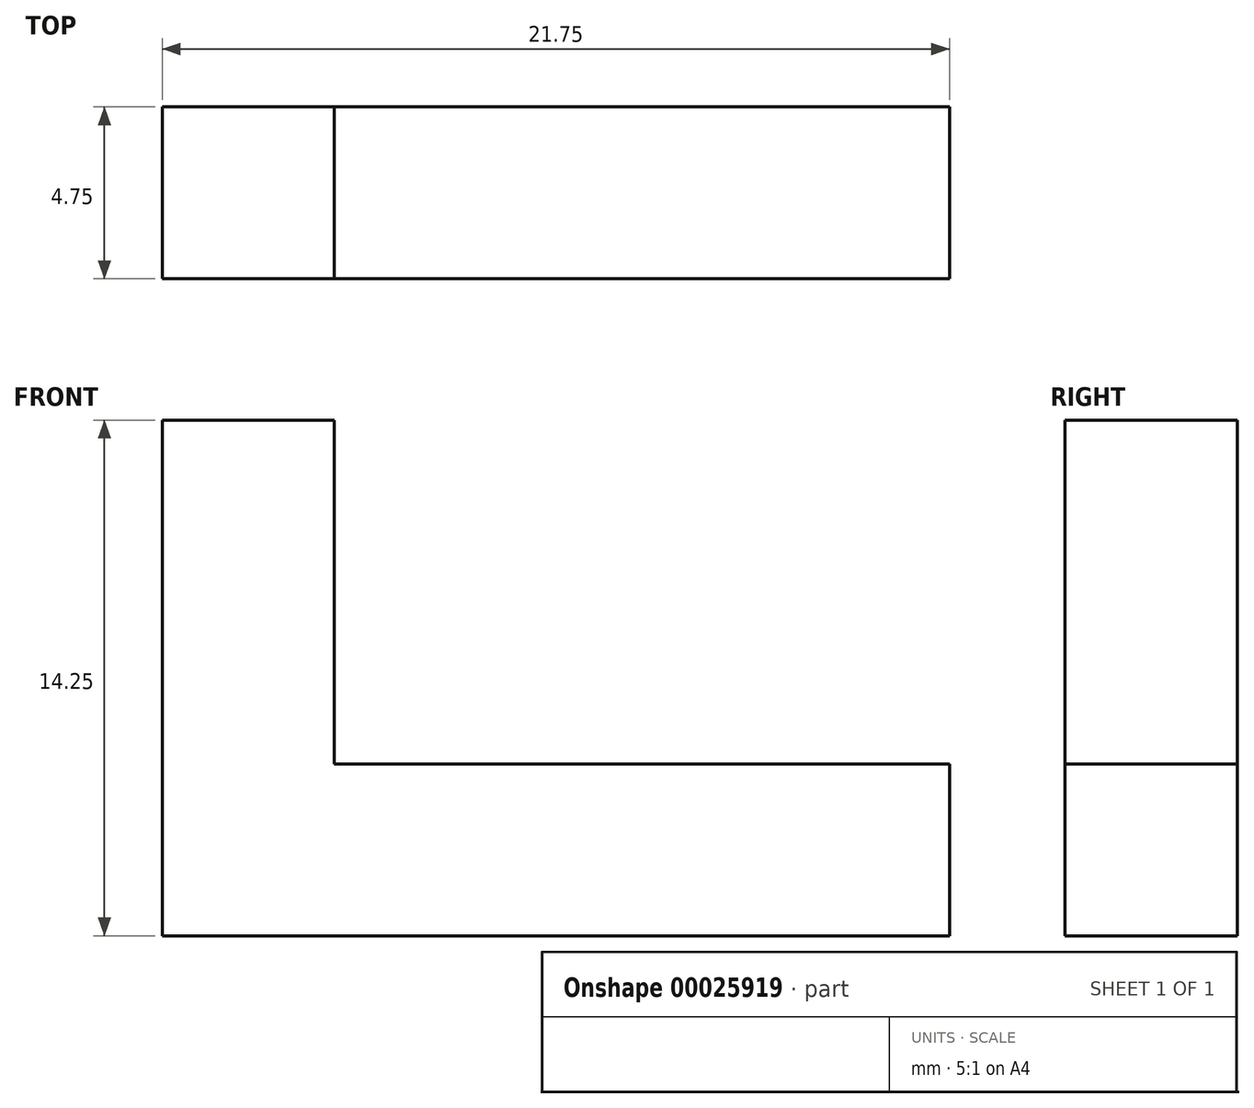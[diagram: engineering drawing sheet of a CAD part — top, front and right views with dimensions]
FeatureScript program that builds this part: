
annotation { "Feature Type Name" : "Feature", "Feature Type Description" : "" }
export const myFeature = defineFeature(function(context is Context, id is Id, definition is map)
    precondition{}
    {
        {
            var Q0;
            Q0=qCreatedBy(makeId("Front.planeOp"),FACE);
            var sketch = newSketch(context, id + "F0", { "sketchPlane" : qUnion([Q0])});
            skLineSegment(sketch, "E0", {"start": v(0, 14.25) * mm, "end": v(0, 0) * mm});
            skLineSegment(sketch, "E1", {"start": v(0, 0) * mm, "end": v(21.75, 0) * mm});
            skLineSegment(sketch, "E2", {"start": v(21.75, 0) * mm, "end": v(21.75, 4.75) * mm});
            skLineSegment(sketch, "E3", {"start": v(21.75, 4.75) * mm, "end": v(4.75, 4.75) * mm});
            skLineSegment(sketch, "E4", {"start": v(4.75, 4.75) * mm, "end": v(4.75, 14.25) * mm});
            skLineSegment(sketch, "E5", {"start": v(4.75, 14.25) * mm, "end": v(0, 14.25) * mm});
            skSolve(sketch);
        }
        {
            var Q0;
            Q0=makeQuery(id+"F0.imprint","IMPRINT",FACE,{"disambiguationData":[TD([[makeQuery(id+"F0.imprint","IMPRINT",EDGE,{"derivedFrom":sQuery(id+"F0.wireOp",EDGE,"E0")}),1.0]])]});
            extrude(context, id + "F1", {"entities" : qUnion([Q0]), "depth" : 4.75 * mm});
        }
    });
